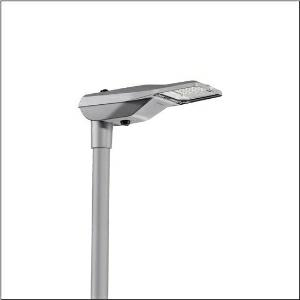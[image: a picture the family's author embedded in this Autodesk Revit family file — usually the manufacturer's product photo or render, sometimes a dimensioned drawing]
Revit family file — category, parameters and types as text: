
# Revit family: streetlight_sl_21_iq_micro___st1_0a_5xe1d51y08cb_5320
name_source: partatom
category: Lighting Fixtures
units: mm (PartAtom-declared; Revit-internal decimal feet)

## family parameters
Cut with Voids When Loaded = No
Host = Face
Light Source = No
Part Type = Normal
Room Calculation Point = No
Round Connector Dimension = Use Diameter
Shared = No

## types (1)
- --- (1 x LED, 2530 lm, 19.1 W, 3000K)
    Apparent Load = 19 VA
    CIE Flux Codes = 37 72 97 100 100
    Color Rendering = 80
    Color Temperature = 3000K
    Default Elevation = 1800 mm
    Description = Streetlight SL 21 iQ micro, mast luminaire, primary light control with lens, of PMMA, primary optical cover: cover, of toughened safety glass, transparent, light distribution: ST1.0a, light emission: direct distribution, primary light characteristic: asymmetric, installation type: post-top, side-entry, LED, High Power LED, rated luminous flux: 2.530lm, luminous efficacy: 133lm/W, light colour: 830, colour temperature: 3000K, control gear: iQ-Street Remote, D4i with power reduction, control: pre-setting: logarithmic dimming characteristic, Street-Remote, Auto-Match, Temp-Guard, Lumen-Switch, Night-Set, Smart-Wire, Light-Fading, Desk-Remote (wireless, voltage-free reading and setting of iQ features in the workshop via application-optimized NFC function/RFID function), optimised constant luminous flux control (CLO 2.0), mains connection: 220..240V, AC, 50/60Hz, start of lifetime: 19W, end of service life: 20W, reduction: 9W, luminaire housing, of diecast aluminium, powder-coated, SITECO metallic grey (DB 702S), corrosivity category C5 high according to DIN EN ISO 12944, please order mast flange separately, inclination adjustable: 0°, 5°, 10°, 15°, sealing non-destructively replaceable, multi-level sealing system, length: 528mm, width: 235mm, height: 110mm, mast flange for spigot size: 42mm (side-entry): 5XC10008XM4, 60/48mm (side-entry/post-top): 5XC10108XM2, 76/60mm (side-entry/post-top): 5XC10108XM1, mounting height: 4..8m, Smart Interface below and above, protection rating (complete): IP66, insulation class (complete): insulation class II (safety insulation), certification: CE, ENEC, ENEC+, VDE, impact resistance: IK10, permissible operating ambient temperature for outdoor applications: -40..+50°C, standard-compliant lighting for roads and squares, packaging unit: 1 piece

Light Distribution: ST1.0a
    Height = 110 mm
    Lamp = 1 x LED
    Lamp Light Flux = 2530 lm
    Lamp Power = 19.1 W
    Lamp count = 1
    Length = 528 mm
    Luminous efficacy = 132 lm/W
    Manufacturer = Siteco
    ModVariant = No
    Model = 5XE1D51Y08CB
    Number of Poles = 1
    OnlyDefault = Yes
    Power Factor = 1
    Product Name = Streetlight SL 21 iQ micro | ST1.0a
    Product group = mast luminaire | pylon top
    ProductGroupID = 6100
    Protection Class = Protection class II
    Protection Degree = IP 66
    RLX_Detail_Level = 1
    RLX_Emergency_Light_Flux = 0 lm
    RLX_Emergency_Type = 0
    RLX_Emergency_Type_DB = No
    RlxData = <blob elided: 98597 chars, md5=40223792>
    Socket = socket
    Standby Power = 0 W
    System Light Flux = 2530 lm
    System Power = 19 W
    Type Comments = factory setting: luminous flux: 100 % | dim-lin: 254 | 387 mA
    Type Image = l_1007239.jpg
    URL = http://relux.com
    VarID = @adj_115503
    Voltage = 0 V
    Weight = 0.00 kg
    Width = 235 mm

## geometry (parser evidence)
native form markers: Blend x4, Sweep x10
no freeform markers — native parametric forms only
